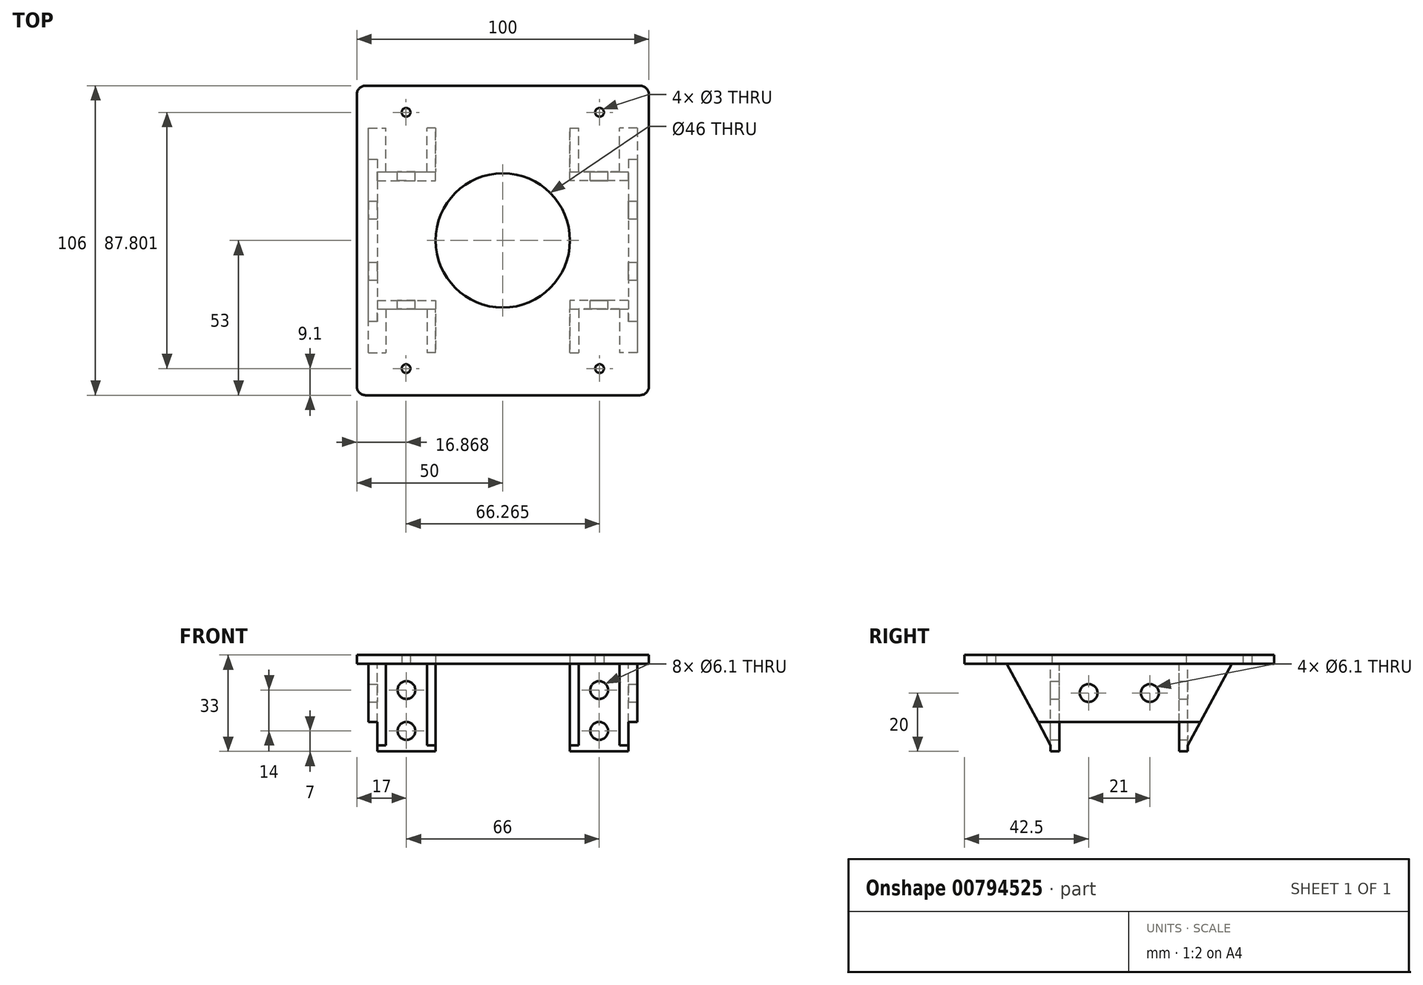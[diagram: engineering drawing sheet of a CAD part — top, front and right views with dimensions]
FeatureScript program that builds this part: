
annotation { "Feature Type Name" : "Feature", "Feature Type Description" : "" }
export const myFeature = defineFeature(function(context is Context, id is Id, definition is map)
    precondition{}
    {
        {
            var Q0;
            Q0=qCreatedBy(makeId("Top.planeOp"),FACE);
            var sketch = newSketch(context, id + "F0", { "sketchPlane" : qUnion([Q0])});
            skCircle(sketch, "E0", {"center": v(0, 0) * mm, "radius": 23 * mm});
            skLineSegment(sketch, "E1.bottom", {"start": v(40, -53) * mm, "end": v(-40, -53) * mm, "construction": true});
            skLineSegment(sketch, "E1.top", {"start": v(40, 53) * mm, "end": v(-40, 53) * mm, "construction": true});
            skLineSegment(sketch, "E1.left", {"start": v(40, -53) * mm, "end": v(40, 53) * mm, "construction": true});
            skLineSegment(sketch, "E1.right", {"start": v(-40, -53) * mm, "end": v(-40, 53) * mm, "construction": true});
            skLineSegment(sketch, "E2.bottom", {"start": v(50, -53) * mm, "end": v(-50, -53) * mm});
            skLineSegment(sketch, "E2.top", {"start": v(50, 53) * mm, "end": v(-50, 53) * mm});
            skLineSegment(sketch, "E2.left", {"start": v(50, -53) * mm, "end": v(50, 53) * mm});
            skLineSegment(sketch, "E2.right", {"start": v(-50, -53) * mm, "end": v(-50, 53) * mm});
            skLineSegment(sketch, "E3", {"start": v(40, 53) * mm, "end": v(-40, -53) * mm, "construction": true});
            skLineSegment(sketch, "E4", {"start": v(-40, 53) * mm, "end": v(40, -53) * mm, "construction": true});
            skCircle(sketch, "E5", {"center": v(33.13, -43.9) * mm, "radius": 1.5 * mm});
            skCircle(sketch, "E6", {"center": v(-33.13, -43.9) * mm, "radius": 1.5 * mm});
            skCircle(sketch, "E7", {"center": v(-33.13, 43.9) * mm, "radius": 1.5 * mm});
            skCircle(sketch, "E8", {"center": v(33.13, 43.9) * mm, "radius": 1.5 * mm});
            skSolve(sketch);
        }
        {
            var Q0;
            Q0=makeQuery(id+"F0.imprint","IMPRINT",FACE,{"disambiguationData":[TD([[makeQuery(id+"F0.imprint","IMPRINT",EDGE,{"derivedFrom":sQuery(id+"F0.wireOp",EDGE,"E0")}),-1.0]])]});
            extrude(context, id + "F1", {"entities" : qUnion([Q0]), "depth" : 3 * mm, "offsetDistance" : 25 * mm});
        }
        {
            var Q0;
            Q0=makeQuery(id+"F1.opExtrude","SWEPT_EDGE",EDGE,{"disambiguationData":[OSD([sQuery(id+"F0.wireOp",EDGE,"E2.bottom"),sQuery(id+"F0.wireOp",EDGE,"E2.right")])]});
            var Q1;
            Q1=makeQuery(id+"F1.opExtrude","SWEPT_EDGE",EDGE,{"disambiguationData":[OSD([sQuery(id+"F0.wireOp",EDGE,"E2.top"),sQuery(id+"F0.wireOp",EDGE,"E2.right")])]});
            var Q2;
            Q2=makeQuery(id+"F1.opExtrude","SWEPT_EDGE",EDGE,{"disambiguationData":[OSD([sQuery(id+"F0.wireOp",EDGE,"E2.top"),sQuery(id+"F0.wireOp",EDGE,"E2.left")])]});
            var Q3;
            Q3=makeQuery(id+"F1.opExtrude","SWEPT_EDGE",EDGE,{"disambiguationData":[OSD([sQuery(id+"F0.wireOp",EDGE,"E2.bottom"),sQuery(id+"F0.wireOp",EDGE,"E2.left")])]});
            fillet(context, id + "F2", {"entities" : qUnion([Q0, Q1, Q2, Q3]), "radius" : 3 * mm, "tangentPropagation" : true, "allowEdgeOverflow" : false});
        }
        {
            var Q0;
            Q0=qCreatedBy(makeId("Top.planeOp"),FACE);
            var sketch = newSketch(context, id + "F3", { "sketchPlane" : qUnion([Q0])});
            skCircle(sketch, "E9.0", {"center": v(0, 0) * mm, "radius": 23 * mm});
            skLineSegment(sketch, "E9.1", {"start": v(50, -53) * mm, "end": v(-50, -53) * mm});
            skLineSegment(sketch, "E9.2", {"start": v(50, 53) * mm, "end": v(-50, 53) * mm});
            skLineSegment(sketch, "E10", {"start": v(-43, -53) * mm, "end": v(-43, 53) * mm, "construction": true});
            skLineSegment(sketch, "E11", {"start": v(43, -53) * mm, "end": v(43, 53) * mm, "construction": true});
            skLineSegment(sketch, "E12", {"start": v(-43, -20.5) * mm, "end": v(43, -20.5) * mm, "construction": true});
            skLineSegment(sketch, "E13", {"start": v(-43, 20.5) * mm, "end": v(43, 20.5) * mm, "construction": true});
            skLineSegment(sketch, "E14", {"start": v(-33, -20.5) * mm, "end": v(-33, 20.5) * mm, "construction": true});
            skLineSegment(sketch, "E15", {"start": v(33, 20.5) * mm, "end": v(33, -20.5) * mm, "construction": true});
            skLineSegment(sketch, "E16.bottom", {"start": v(-43, 20.5) * mm, "end": v(-23, 20.5) * mm});
            skLineSegment(sketch, "E16.top", {"start": v(-43, 23.5) * mm, "end": v(-23, 23.5) * mm});
            skLineSegment(sketch, "E16.left", {"start": v(-43, 20.5) * mm, "end": v(-43, 23.5) * mm});
            skLineSegment(sketch, "E16.right", {"start": v(-23, 20.5) * mm, "end": v(-23, 23.5) * mm});
            skLineSegment(sketch, "E17.bottom", {"start": v(-43, -20.5) * mm, "end": v(-23, -20.5) * mm});
            skLineSegment(sketch, "E17.top", {"start": v(-43, -23.5) * mm, "end": v(-23, -23.5) * mm});
            skLineSegment(sketch, "E17.left", {"start": v(-43, -20.5) * mm, "end": v(-43, -23.5) * mm});
            skLineSegment(sketch, "E17.right", {"start": v(-23, -20.5) * mm, "end": v(-23, -23.5) * mm});
            skLineSegment(sketch, "E18.bottom", {"start": v(43, -20.5) * mm, "end": v(23, -20.5) * mm});
            skLineSegment(sketch, "E18.top", {"start": v(43, -23.5) * mm, "end": v(23, -23.5) * mm});
            skLineSegment(sketch, "E18.left", {"start": v(43, -20.5) * mm, "end": v(43, -23.5) * mm});
            skLineSegment(sketch, "E18.right", {"start": v(23, -20.5) * mm, "end": v(23, -23.5) * mm});
            skLineSegment(sketch, "E19.bottom", {"start": v(43, 20.5) * mm, "end": v(23, 20.5) * mm});
            skLineSegment(sketch, "E19.top", {"start": v(43, 23.5) * mm, "end": v(23, 23.5) * mm});
            skLineSegment(sketch, "E19.left", {"start": v(43, 20.5) * mm, "end": v(43, 23.5) * mm});
            skLineSegment(sketch, "E19.right", {"start": v(23, 20.5) * mm, "end": v(23, 23.5) * mm});
            skLineSegment(sketch, "E20.bottom", {"start": v(-43, -23.5) * mm, "end": v(-46, -23.5) * mm});
            skLineSegment(sketch, "E20.top", {"start": v(-43, 23.5) * mm, "end": v(-46, 23.5) * mm});
            skLineSegment(sketch, "E20.left", {"start": v(-43, -23.5) * mm, "end": v(-43, 23.5) * mm});
            skLineSegment(sketch, "E20.right", {"start": v(-46, -23.5) * mm, "end": v(-46, 23.5) * mm});
            skLineSegment(sketch, "E21.bottom", {"start": v(43, 23.5) * mm, "end": v(46, 23.5) * mm});
            skLineSegment(sketch, "E21.top", {"start": v(43, -23.5) * mm, "end": v(46, -23.5) * mm});
            skLineSegment(sketch, "E21.left", {"start": v(43, 23.5) * mm, "end": v(43, -23.5) * mm});
            skLineSegment(sketch, "E21.right", {"start": v(46, 23.5) * mm, "end": v(46, -23.5) * mm});
            skLineSegment(sketch, "E22.bottom", {"start": v(-43, 23.5) * mm, "end": v(-40, 23.5) * mm});
            skLineSegment(sketch, "E22.top", {"start": v(-43, 38.5) * mm, "end": v(-40, 38.5) * mm});
            skLineSegment(sketch, "E22.left", {"start": v(-43, 23.5) * mm, "end": v(-43, 38.5) * mm});
            skLineSegment(sketch, "E22.right", {"start": v(-40, 23.5) * mm, "end": v(-40, 38.5) * mm});
            skLineSegment(sketch, "E23.bottom", {"start": v(-23, 23.5) * mm, "end": v(-26, 23.5) * mm});
            skLineSegment(sketch, "E23.top", {"start": v(-23, 38.5) * mm, "end": v(-26, 38.5) * mm});
            skLineSegment(sketch, "E23.left", {"start": v(-23, 23.5) * mm, "end": v(-23, 38.5) * mm});
            skLineSegment(sketch, "E23.right", {"start": v(-26, 23.5) * mm, "end": v(-26, 38.5) * mm});
            skLineSegment(sketch, "E24.bottom", {"start": v(23, 23.5) * mm, "end": v(26, 23.5) * mm});
            skLineSegment(sketch, "E24.top", {"start": v(23, 38.5) * mm, "end": v(26, 38.5) * mm});
            skLineSegment(sketch, "E24.left", {"start": v(23, 23.5) * mm, "end": v(23, 38.5) * mm});
            skLineSegment(sketch, "E24.right", {"start": v(26, 23.5) * mm, "end": v(26, 38.5) * mm});
            skLineSegment(sketch, "E25.bottom", {"start": v(43, 23.5) * mm, "end": v(40, 23.5) * mm});
            skLineSegment(sketch, "E25.top", {"start": v(43, 38.5) * mm, "end": v(40, 38.5) * mm});
            skLineSegment(sketch, "E25.left", {"start": v(43, 23.5) * mm, "end": v(43, 38.5) * mm});
            skLineSegment(sketch, "E25.right", {"start": v(40, 23.5) * mm, "end": v(40, 38.5) * mm});
            skLineSegment(sketch, "E26.bottom", {"start": v(23, -23.5) * mm, "end": v(26, -23.5) * mm});
            skLineSegment(sketch, "E26.top", {"start": v(23, -38.5) * mm, "end": v(26, -38.5) * mm});
            skLineSegment(sketch, "E26.left", {"start": v(23, -23.5) * mm, "end": v(23, -38.5) * mm});
            skLineSegment(sketch, "E26.right", {"start": v(26, -23.5) * mm, "end": v(26, -38.5) * mm});
            skLineSegment(sketch, "E27.bottom", {"start": v(43, -23.5) * mm, "end": v(40, -23.5) * mm});
            skLineSegment(sketch, "E27.top", {"start": v(43, -38.5) * mm, "end": v(40, -38.5) * mm});
            skLineSegment(sketch, "E27.left", {"start": v(43, -23.5) * mm, "end": v(43, -38.5) * mm});
            skLineSegment(sketch, "E27.right", {"start": v(40, -23.5) * mm, "end": v(40, -38.5) * mm});
            skLineSegment(sketch, "E28.bottom", {"start": v(-23, -23.5) * mm, "end": v(-26, -23.5) * mm});
            skLineSegment(sketch, "E28.top", {"start": v(-23, -38.5) * mm, "end": v(-26, -38.5) * mm});
            skLineSegment(sketch, "E28.left", {"start": v(-23, -23.5) * mm, "end": v(-23, -38.5) * mm});
            skLineSegment(sketch, "E28.right", {"start": v(-26, -23.5) * mm, "end": v(-26, -38.5) * mm});
            skLineSegment(sketch, "E29.bottom", {"start": v(-43, -23.5) * mm, "end": v(-40, -23.5) * mm});
            skLineSegment(sketch, "E29.top", {"start": v(-43, -38.5) * mm, "end": v(-40, -38.5) * mm});
            skLineSegment(sketch, "E29.left", {"start": v(-43, -23.5) * mm, "end": v(-43, -38.5) * mm});
            skLineSegment(sketch, "E29.right", {"start": v(-40, -23.5) * mm, "end": v(-40, -38.5) * mm});
            skSolve(sketch);
        }
        {
            var Q0;
            Q0=makeQuery(id+"F3.imprint","IMPRINT",FACE,{"disambiguationData":[TD([[makeQuery(id+"F3.imprint","IMPRINT",EDGE,{"derivedFrom":sQuery(id+"F3.wireOp",EDGE,"E17.bottom")}),-1.0]])]});
            var Q1;
            Q1=makeQuery(id+"F3.imprint","IMPRINT",FACE,{"disambiguationData":[TD([[makeQuery(id+"F3.imprint","IMPRINT",EDGE,{"derivedFrom":sQuery(id+"F3.wireOp",EDGE,"E16.bottom")}),1.0]])]});
            var Q2;
            Q2=makeQuery(id+"F3.imprint","IMPRINT",FACE,{"disambiguationData":[TD([[makeQuery(id+"F3.imprint","IMPRINT",EDGE,{"derivedFrom":sQuery(id+"F3.wireOp",EDGE,"E19.bottom")}),-1.0]])]});
            var Q3;
            Q3=makeQuery(id+"F3.imprint","IMPRINT",FACE,{"disambiguationData":[TD([[makeQuery(id+"F3.imprint","IMPRINT",EDGE,{"derivedFrom":sQuery(id+"F3.wireOp",EDGE,"E18.bottom")}),1.0]])]});
            extrude(context, id + "F4", {"entities" : qUnion([Q0, Q1, Q2, Q3]), "operationType" : NewBodyOperationType.ADD, "oppositeDirection" : true, "depth" : 28 * mm, "offsetDistance" : 25 * mm});
        }
        {
            var Q0;
            Q0=makeQuery(id+"F3.imprint","IMPRINT",FACE,{"disambiguationData":[TD([[makeQuery(id+"F3.imprint","IMPRINT",EDGE,{"derivedFrom":sQuery(id+"F3.wireOp",EDGE,"E18.left")}),1.0]])]});
            var Q1;
            Q1=makeQuery(id+"F3.imprint","IMPRINT",FACE,{"disambiguationData":[TD([[makeQuery(id+"F3.imprint","IMPRINT",EDGE,{"derivedFrom":sQuery(id+"F3.wireOp",EDGE,"E16.left")}),1.0]])]});
            extrude(context, id + "F5", {"entities" : qUnion([Q0, Q1]), "operationType" : NewBodyOperationType.ADD, "oppositeDirection" : true, "depth" : 20 * mm, "offsetDistance" : 25 * mm});
        }
        {
            var Q0;
            Q0=makeQuery(id+"F3.imprint","IMPRINT",FACE,{"disambiguationData":[TD([[makeQuery(id+"F3.imprint","IMPRINT",EDGE,{"derivedFrom":sQuery(id+"F3.wireOp",EDGE,"E22.top")}),-1.0]])]});
            var Q1;
            Q1=makeQuery(id+"F3.imprint","IMPRINT",FACE,{"disambiguationData":[TD([[makeQuery(id+"F3.imprint","IMPRINT",EDGE,{"derivedFrom":sQuery(id+"F3.wireOp",EDGE,"E23.top")}),1.0]])]});
            var Q2;
            Q2=makeQuery(id+"F3.imprint","IMPRINT",FACE,{"disambiguationData":[TD([[makeQuery(id+"F3.imprint","IMPRINT",EDGE,{"derivedFrom":sQuery(id+"F3.wireOp",EDGE,"E24.top")}),-1.0]])]});
            var Q3;
            Q3=makeQuery(id+"F3.imprint","IMPRINT",FACE,{"disambiguationData":[TD([[makeQuery(id+"F3.imprint","IMPRINT",EDGE,{"derivedFrom":sQuery(id+"F3.wireOp",EDGE,"E25.top")}),1.0]])]});
            var Q4;
            Q4=makeQuery(id+"F3.imprint","IMPRINT",FACE,{"disambiguationData":[TD([[makeQuery(id+"F3.imprint","IMPRINT",EDGE,{"derivedFrom":sQuery(id+"F3.wireOp",EDGE,"E29.top")}),1.0]])]});
            var Q5;
            Q5=makeQuery(id+"F3.imprint","IMPRINT",FACE,{"disambiguationData":[TD([[makeQuery(id+"F3.imprint","IMPRINT",EDGE,{"derivedFrom":sQuery(id+"F3.wireOp",EDGE,"E28.top")}),-1.0]])]});
            var Q6;
            Q6=makeQuery(id+"F3.imprint","IMPRINT",FACE,{"disambiguationData":[TD([[makeQuery(id+"F3.imprint","IMPRINT",EDGE,{"derivedFrom":sQuery(id+"F3.wireOp",EDGE,"E26.top")}),1.0]])]});
            var Q7;
            Q7=makeQuery(id+"F3.imprint","IMPRINT",FACE,{"disambiguationData":[TD([[makeQuery(id+"F3.imprint","IMPRINT",EDGE,{"derivedFrom":sQuery(id+"F3.wireOp",EDGE,"E27.top")}),-1.0]])]});
            extrude(context, id + "F6", {"entities" : qUnion([Q0, Q1, Q2, Q3, Q4, Q5, Q6, Q7]), "operationType" : NewBodyOperationType.ADD, "oppositeDirection" : true, "depth" : 28 * mm, "offsetDistance" : 25 * mm});
        }
        {
            var Q0;
            {var subQ1=sQuery(id+"F3.wireOp",EDGE,"E20.bottom");var subQ2=sQuery(id+"F3.wireOp",EDGE,"E17.left");Q0=makeQuery(id+"F6.boolean.opBoolean","SPLIT",FACE,{"disambiguationData":[TD([makeQuery(id+"F4.opExtrude","SWEPT_FACE",FACE,{"disambiguationData":[OSD([subQ2])]})])],"derivedFrom":makeQuery(id+"F5.boolean.opBoolean","MERGE",FACE,{"derivedFrom":[makeQuery(id+"F4.opExtrude","SWEPT_FACE",FACE,{"disambiguationData":[OSD([sQuery(id+"F3.wireOp",EDGE,"E17.top")])]}),makeQuery(id+"F5.opExtrude","SWEPT_FACE",FACE,{"disambiguationData":[OSD([subQ1])]})]})});}
            var Q1;
            {var subQ1=sQuery(id+"F3.wireOp",EDGE,"E21.top");var subQ2=sQuery(id+"F3.wireOp",EDGE,"E18.left");Q1=makeQuery(id+"F6.boolean.opBoolean","SPLIT",FACE,{"disambiguationData":[TD([makeQuery(id+"F4.opExtrude","SWEPT_FACE",FACE,{"disambiguationData":[OSD([subQ2])]})])],"derivedFrom":makeQuery(id+"F5.boolean.opBoolean","MERGE",FACE,{"derivedFrom":[makeQuery(id+"F4.opExtrude","SWEPT_FACE",FACE,{"disambiguationData":[OSD([sQuery(id+"F3.wireOp",EDGE,"E18.top")])]}),makeQuery(id+"F5.opExtrude","SWEPT_FACE",FACE,{"disambiguationData":[OSD([subQ1])]})]})});}
            var Q2;
            Q2=makeQuery(id+"F6.opExtrude","SWEPT_FACE",FACE,{"disambiguationData":[OSD([sQuery(id+"F3.wireOp",EDGE,"E29.top")])]});
            var Q3;
            Q3=makeQuery(id+"F6.opExtrude","SWEPT_FACE",FACE,{"disambiguationData":[OSD([sQuery(id+"F3.wireOp",EDGE,"E22.top")])]});
            extrude(context, id + "F7", {"entities" : qUnion([Q0, Q1]), "operationType" : NewBodyOperationType.ADD, "endBound" : BoundingType.UP_TO_SURFACE, "depth" : 25 * mm, "endBoundEntityFace" : qUnion([Q2]), "offsetDistance" : 25 * mm, "hasSecondDirection" : true, "secondDirectionBound" : SecondDirectionBoundingType.UP_TO_SURFACE, "secondDirectionOppositeDirection" : true, "secondDirectionDepth" : 25 * mm, "secondDirectionBoundEntityFace" : qUnion([Q3])});
        }
        {
            var Q0;
            Q0=makeQuery(id+"F6.opExtrude","SWEPT_FACE",FACE,{"disambiguationData":[OSD([sQuery(id+"F3.wireOp",EDGE,"E23.right")])]});
            var sketch = newSketch(context, id + "F8", { "sketchPlane" : qUnion([Q0])});
            skLineSegment(sketch, "E30", {"start": v(-38.5, 0) * mm, "end": v(-23.5, -28) * mm});
            skSolve(sketch);
        }
        {
            var Q0;
            Q0=makeQuery(id+"F8.imprint","IMPRINT",FACE,{"disambiguationData":[TD([[makeQuery(id+"F8.imprint","IMPRINT",EDGE,{"derivedFrom":sQuery(id+"F8.wireOp",EDGE,"E30")}),-1.0]])]});
            var Q1;
            {var subQ0=sQuery(id+"F3.wireOp",EDGE,"E20.right");Q1=makeQuery(id+"F7.boolean.opBoolean","MERGE",FACE,{"derivedFrom":[makeQuery(id+"F5.opExtrude","SWEPT_FACE",FACE,{"disambiguationData":[OSD([subQ0])]}),makeQuery(id+"F7.opExtrude","SWEPT_FACE",FACE,{"disambiguationData":[OSD([sQuery(id+"F3.wireOp",EDGE,"E20.bottom"),subQ0])]})]});}
            var Q2;
            {var subQ0=sQuery(id+"F3.wireOp",EDGE,"E21.right");Q2=makeQuery(id+"F7.boolean.opBoolean","MERGE",FACE,{"derivedFrom":[makeQuery(id+"F5.opExtrude","SWEPT_FACE",FACE,{"disambiguationData":[OSD([subQ0])]}),makeQuery(id+"F7.opExtrude","SWEPT_FACE",FACE,{"disambiguationData":[OSD([sQuery(id+"F3.wireOp",EDGE,"E21.top"),subQ0])]})]});}
            extrude(context, id + "F9", {"entities" : qUnion([Q0]), "operationType" : NewBodyOperationType.REMOVE, "endBound" : BoundingType.UP_TO_SURFACE, "depth" : 25 * mm, "endBoundEntityFace" : qUnion([Q1]), "offsetDistance" : 25 * mm, "hasSecondDirection" : true, "secondDirectionBound" : SecondDirectionBoundingType.UP_TO_SURFACE, "secondDirectionOppositeDirection" : true, "secondDirectionDepth" : 25 * mm, "secondDirectionBoundEntityFace" : qUnion([Q2])});
        }
        {
            var Q0;
            Q0=makeQuery(id+"F6.opExtrude","SWEPT_FACE",FACE,{"disambiguationData":[OSD([sQuery(id+"F3.wireOp",EDGE,"E28.right")])]});
            var sketch = newSketch(context, id + "F10", { "sketchPlane" : qUnion([Q0])});
            skLineSegment(sketch, "E31", {"start": v(23.5, -28) * mm, "end": v(38.5, 0) * mm});
            skSolve(sketch);
        }
        {
            var Q0;
            Q0=makeQuery(id+"F10.imprint","IMPRINT",FACE,{"disambiguationData":[TD([[makeQuery(id+"F10.imprint","IMPRINT",EDGE,{"derivedFrom":sQuery(id+"F10.wireOp",EDGE,"E31")}),-1.0]])]});
            var Q1;
            {var subQ0=sQuery(id+"F3.wireOp",EDGE,"E20.right");Q1=makeQuery(id+"F7.boolean.opBoolean","MERGE",FACE,{"derivedFrom":[makeQuery(id+"F5.opExtrude","SWEPT_FACE",FACE,{"disambiguationData":[OSD([subQ0])]}),makeQuery(id+"F7.opExtrude","SWEPT_FACE",FACE,{"disambiguationData":[OSD([sQuery(id+"F3.wireOp",EDGE,"E20.bottom"),subQ0])]})]});}
            var Q2;
            {var subQ0=sQuery(id+"F3.wireOp",EDGE,"E21.right");Q2=makeQuery(id+"F7.boolean.opBoolean","MERGE",FACE,{"derivedFrom":[makeQuery(id+"F5.opExtrude","SWEPT_FACE",FACE,{"disambiguationData":[OSD([subQ0])]}),makeQuery(id+"F7.opExtrude","SWEPT_FACE",FACE,{"disambiguationData":[OSD([sQuery(id+"F3.wireOp",EDGE,"E21.top"),subQ0])]})]});}
            extrude(context, id + "F11", {"entities" : qUnion([Q0]), "operationType" : NewBodyOperationType.REMOVE, "endBound" : BoundingType.UP_TO_SURFACE, "depth" : 25 * mm, "endBoundEntityFace" : qUnion([Q1]), "offsetDistance" : 25 * mm, "hasSecondDirection" : true, "secondDirectionBound" : SecondDirectionBoundingType.UP_TO_SURFACE, "secondDirectionOppositeDirection" : true, "secondDirectionDepth" : 25 * mm, "secondDirectionBoundEntityFace" : qUnion([Q2])});
        }
        {
            var Q0;
            {var subQ1=sQuery(id+"F3.wireOp",EDGE,"E16.top");var subQ2=sQuery(id+"F3.wireOp",EDGE,"E22.right");Q0=makeQuery(id+"F6.boolean.opBoolean","SPLIT",FACE,{"disambiguationData":[TD([makeQuery(id+"F6.opExtrude","SWEPT_FACE",FACE,{"disambiguationData":[OSD([subQ2])]})])],"derivedFrom":makeQuery(id+"F5.boolean.opBoolean","MERGE",FACE,{"derivedFrom":[makeQuery(id+"F4.opExtrude","SWEPT_FACE",FACE,{"disambiguationData":[OSD([subQ1])]}),makeQuery(id+"F5.opExtrude","SWEPT_FACE",FACE,{"disambiguationData":[OSD([sQuery(id+"F3.wireOp",EDGE,"E20.top")])]})]})});}
            var sketch = newSketch(context, id + "F12", { "sketchPlane" : qUnion([Q0])});
            skLineSegment(sketch, "E32", {"start": v(33, -28) * mm, "end": v(33, 0) * mm, "construction": true});
            skCircle(sketch, "E33", {"center": v(33, -23) * mm, "radius": 3.05 * mm});
            skCircle(sketch, "E34", {"center": v(33, -9) * mm, "radius": 3.05 * mm});
            skSolve(sketch);
        }
        {
            var Q0;
            {var subQ1=sQuery(id+"F3.wireOp",EDGE,"E19.top");var subQ2=sQuery(id+"F3.wireOp",EDGE,"E24.right");Q0=makeQuery(id+"F6.boolean.opBoolean","SPLIT",FACE,{"disambiguationData":[TD([makeQuery(id+"F6.opExtrude","SWEPT_FACE",FACE,{"disambiguationData":[OSD([subQ2])]})])],"derivedFrom":makeQuery(id+"F5.boolean.opBoolean","MERGE",FACE,{"derivedFrom":[makeQuery(id+"F4.opExtrude","SWEPT_FACE",FACE,{"disambiguationData":[OSD([subQ1])]}),makeQuery(id+"F5.opExtrude","SWEPT_FACE",FACE,{"disambiguationData":[OSD([sQuery(id+"F3.wireOp",EDGE,"E21.bottom")])]})]})});}
            var sketch = newSketch(context, id + "F13", { "sketchPlane" : qUnion([Q0])});
            skLineSegment(sketch, "E35", {"start": v(-33, 0) * mm, "end": v(-33, -28) * mm, "construction": true});
            skCircle(sketch, "E36", {"center": v(-33, -23) * mm, "radius": 3.05 * mm});
            skCircle(sketch, "E37", {"center": v(-33, -9) * mm, "radius": 3.05 * mm});
            skSolve(sketch);
        }
        {
            var Q0;
            Q0=makeQuery(id+"F12.imprint","IMPRINT",FACE,{"disambiguationData":[TD([[makeQuery(id+"F12.imprint","IMPRINT",EDGE,{"derivedFrom":sQuery(id+"F12.wireOp",EDGE,"E33")}),1.0]])]});
            var Q1;
            Q1=makeQuery(id+"F12.imprint","IMPRINT",FACE,{"disambiguationData":[TD([[makeQuery(id+"F12.imprint","IMPRINT",EDGE,{"derivedFrom":sQuery(id+"F12.wireOp",EDGE,"E34")}),1.0]])]});
            var Q2;
            Q2=makeQuery(id+"F13.imprint","IMPRINT",FACE,{"disambiguationData":[TD([[makeQuery(id+"F13.imprint","IMPRINT",EDGE,{"derivedFrom":sQuery(id+"F13.wireOp",EDGE,"E37")}),1.0]])]});
            var Q3;
            Q3=makeQuery(id+"F13.imprint","IMPRINT",FACE,{"disambiguationData":[TD([[makeQuery(id+"F13.imprint","IMPRINT",EDGE,{"derivedFrom":sQuery(id+"F13.wireOp",EDGE,"E36")}),1.0]])]});
            var Q4;
            {var subQ1=sQuery(id+"F3.wireOp",EDGE,"E17.top");var subQ2=sQuery(id+"F3.wireOp",EDGE,"E28.right");Q4=makeQuery(id+"F6.boolean.opBoolean","SPLIT",FACE,{"disambiguationData":[TD([makeQuery(id+"F6.opExtrude","SWEPT_FACE",FACE,{"disambiguationData":[OSD([subQ2])]})])],"derivedFrom":makeQuery(id+"F5.boolean.opBoolean","MERGE",FACE,{"derivedFrom":[makeQuery(id+"F4.opExtrude","SWEPT_FACE",FACE,{"disambiguationData":[OSD([subQ1])]}),makeQuery(id+"F5.opExtrude","SWEPT_FACE",FACE,{"disambiguationData":[OSD([sQuery(id+"F3.wireOp",EDGE,"E20.bottom")])]})]})});}
            extrude(context, id + "F14", {"entities" : qUnion([Q0, Q1, Q2, Q3]), "operationType" : NewBodyOperationType.REMOVE, "endBound" : BoundingType.UP_TO_SURFACE, "oppositeDirection" : true, "depth" : 25 * mm, "endBoundEntityFace" : qUnion([Q4]), "offsetDistance" : 25 * mm});
        }
        {
            var Q0;
            Q0=makeQuery(id+"F5.opExtrude","SWEPT_FACE",FACE,{"disambiguationData":[OSD([sQuery(id+"F3.wireOp",EDGE,"E16.left"),sQuery(id+"F3.wireOp",EDGE,"E17.left"),sQuery(id+"F3.wireOp",EDGE,"E20.left")])]});
            var sketch = newSketch(context, id + "F15", { "sketchPlane" : qUnion([Q0])});
            skLineSegment(sketch, "E38", {"start": v(-10.5, 0) * mm, "end": v(-10.5, -20) * mm, "construction": true});
            skLineSegment(sketch, "E39", {"start": v(10.5, 0) * mm, "end": v(10.5, -20) * mm, "construction": true});
            skCircle(sketch, "E40", {"center": v(10.5, -10) * mm, "radius": 3.05 * mm});
            skCircle(sketch, "E41", {"center": v(-10.5, -10) * mm, "radius": 3.05 * mm});
            skSolve(sketch);
        }
        {
            var Q0;
            Q0=makeQuery(id+"F15.imprint","IMPRINT",FACE,{"disambiguationData":[TD([[makeQuery(id+"F15.imprint","IMPRINT",EDGE,{"derivedFrom":sQuery(id+"F15.wireOp",EDGE,"E40")}),1.0]])]});
            var Q1;
            Q1=makeQuery(id+"F15.imprint","IMPRINT",FACE,{"disambiguationData":[TD([[makeQuery(id+"F15.imprint","IMPRINT",EDGE,{"derivedFrom":sQuery(id+"F15.wireOp",EDGE,"E41")}),1.0]])]});
            var Q2;
            {var subQ0=sQuery(id+"F3.wireOp",EDGE,"E20.right");Q2=makeQuery(id+"F7.boolean.opBoolean","MERGE",FACE,{"derivedFrom":[makeQuery(id+"F5.opExtrude","SWEPT_FACE",FACE,{"disambiguationData":[OSD([subQ0])]}),makeQuery(id+"F7.opExtrude","SWEPT_FACE",FACE,{"disambiguationData":[OSD([sQuery(id+"F3.wireOp",EDGE,"E20.bottom"),subQ0])]})]});}
            var Q3;
            {var subQ0=sQuery(id+"F3.wireOp",EDGE,"E21.right");Q3=makeQuery(id+"F7.boolean.opBoolean","MERGE",FACE,{"derivedFrom":[makeQuery(id+"F5.opExtrude","SWEPT_FACE",FACE,{"disambiguationData":[OSD([subQ0])]}),makeQuery(id+"F7.opExtrude","SWEPT_FACE",FACE,{"disambiguationData":[OSD([sQuery(id+"F3.wireOp",EDGE,"E21.top"),subQ0])]})]});}
            extrude(context, id + "F16", {"entities" : qUnion([Q0, Q1]), "operationType" : NewBodyOperationType.REMOVE, "endBound" : BoundingType.UP_TO_SURFACE, "oppositeDirection" : true, "depth" : 25 * mm, "endBoundEntityFace" : qUnion([Q2]), "offsetDistance" : 25 * mm, "hasSecondDirection" : true, "secondDirectionBound" : SecondDirectionBoundingType.UP_TO_SURFACE, "secondDirectionOppositeDirection" : false, "secondDirectionDepth" : 25 * mm, "secondDirectionBoundEntityFace" : qUnion([Q3])});
        }
        {
            var Q0;
            {var subQ0=sQuery(id+"F3.wireOp",EDGE,"E18.top");Q0=makeQuery(id+"F6.boolean.opBoolean","MERGE",FACE,{"derivedFrom":[makeQuery(id+"F4.opExtrude","CAP_FACE",FACE,{"disambiguationData":[OSD([sQuery(id+"F3.wireOp",EDGE,"E18.bottom"),subQ0,sQuery(id+"F3.wireOp",EDGE,"E18.left"),sQuery(id+"F3.wireOp",EDGE,"E18.right")])],"isStart":false}),makeQuery(id+"F6.opExtrude","CAP_FACE",FACE,{"disambiguationData":[OSD([subQ0,sQuery(id+"F3.wireOp",EDGE,"E27.top"),sQuery(id+"F3.wireOp",EDGE,"E27.left"),sQuery(id+"F3.wireOp",EDGE,"E27.right")])],"isStart":false}),makeQuery(id+"F6.opExtrude","CAP_FACE",FACE,{"disambiguationData":[OSD([subQ0,sQuery(id+"F3.wireOp",EDGE,"E26.top"),sQuery(id+"F3.wireOp",EDGE,"E26.left"),sQuery(id+"F3.wireOp",EDGE,"E26.right")])],"isStart":false})]});}
            var Q1;
            {var subQ0=sQuery(id+"F3.wireOp",EDGE,"E17.top");Q1=makeQuery(id+"F6.boolean.opBoolean","MERGE",FACE,{"derivedFrom":[makeQuery(id+"F4.opExtrude","CAP_FACE",FACE,{"disambiguationData":[OSD([sQuery(id+"F3.wireOp",EDGE,"E17.bottom"),subQ0,sQuery(id+"F3.wireOp",EDGE,"E17.left"),sQuery(id+"F3.wireOp",EDGE,"E17.right")])],"isStart":false}),makeQuery(id+"F6.opExtrude","CAP_FACE",FACE,{"disambiguationData":[OSD([subQ0,sQuery(id+"F3.wireOp",EDGE,"E28.top"),sQuery(id+"F3.wireOp",EDGE,"E28.left"),sQuery(id+"F3.wireOp",EDGE,"E28.right")])],"isStart":false}),makeQuery(id+"F6.opExtrude","CAP_FACE",FACE,{"disambiguationData":[OSD([subQ0,sQuery(id+"F3.wireOp",EDGE,"E29.top"),sQuery(id+"F3.wireOp",EDGE,"E29.left"),sQuery(id+"F3.wireOp",EDGE,"E29.right")])],"isStart":false})]});}
            var Q2;
            {var subQ0=sQuery(id+"F3.wireOp",EDGE,"E16.top");Q2=makeQuery(id+"F6.boolean.opBoolean","MERGE",FACE,{"derivedFrom":[makeQuery(id+"F4.opExtrude","CAP_FACE",FACE,{"disambiguationData":[OSD([sQuery(id+"F3.wireOp",EDGE,"E16.bottom"),subQ0,sQuery(id+"F3.wireOp",EDGE,"E16.left"),sQuery(id+"F3.wireOp",EDGE,"E16.right")])],"isStart":false}),makeQuery(id+"F6.opExtrude","CAP_FACE",FACE,{"disambiguationData":[OSD([subQ0,sQuery(id+"F3.wireOp",EDGE,"E22.top"),sQuery(id+"F3.wireOp",EDGE,"E22.left"),sQuery(id+"F3.wireOp",EDGE,"E22.right")])],"isStart":false}),makeQuery(id+"F6.opExtrude","CAP_FACE",FACE,{"disambiguationData":[OSD([subQ0,sQuery(id+"F3.wireOp",EDGE,"E23.top"),sQuery(id+"F3.wireOp",EDGE,"E23.left"),sQuery(id+"F3.wireOp",EDGE,"E23.right")])],"isStart":false})]});}
            var Q3;
            {var subQ0=sQuery(id+"F3.wireOp",EDGE,"E19.top");Q3=makeQuery(id+"F6.boolean.opBoolean","MERGE",FACE,{"derivedFrom":[makeQuery(id+"F4.opExtrude","CAP_FACE",FACE,{"disambiguationData":[OSD([sQuery(id+"F3.wireOp",EDGE,"E19.bottom"),subQ0,sQuery(id+"F3.wireOp",EDGE,"E19.left"),sQuery(id+"F3.wireOp",EDGE,"E19.right")])],"isStart":false}),makeQuery(id+"F6.opExtrude","CAP_FACE",FACE,{"disambiguationData":[OSD([subQ0,sQuery(id+"F3.wireOp",EDGE,"E25.top"),sQuery(id+"F3.wireOp",EDGE,"E25.left"),sQuery(id+"F3.wireOp",EDGE,"E25.right")])],"isStart":false}),makeQuery(id+"F6.opExtrude","CAP_FACE",FACE,{"disambiguationData":[OSD([subQ0,sQuery(id+"F3.wireOp",EDGE,"E24.top"),sQuery(id+"F3.wireOp",EDGE,"E24.left"),sQuery(id+"F3.wireOp",EDGE,"E24.right")])],"isStart":false})]});}
            extrude(context, id + "F17", {"entities" : qUnion([Q0, Q1, Q2, Q3]), "operationType" : NewBodyOperationType.ADD, "depth" : 2 * mm, "offsetDistance" : 25 * mm});
        }
    });
